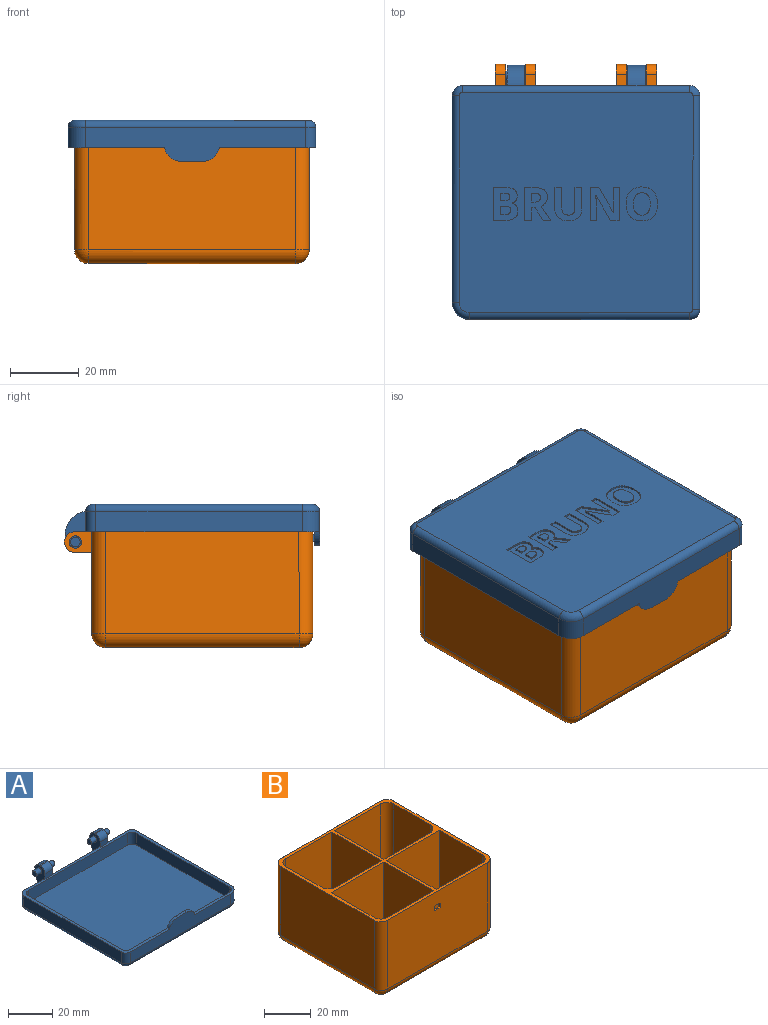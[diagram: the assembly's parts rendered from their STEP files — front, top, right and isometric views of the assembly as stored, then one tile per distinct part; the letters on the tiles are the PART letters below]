
ASSEMBLY  parts=2 mates=1
PART A: 157 faces, bbox 72.7x74.7x14 mm
  f0: plane 13x6mm, normal (0,1,0), area 78mm2, adj f1,f11,f28,f131
  f1: plane 72.3x68.3mm, normal (0,0,1), area 380.4mm2, adj f0,f2,f4,f5,f6,f7,f8,f9
  f2: plane 30.3x6mm, normal (0,1,0), area 181.8mm2, adj f1,f28,f127,f133
  f3: plane 68.3x64.3mm, normal (0,0,-1), area 4104.8mm2, adj f21,f22,f23,f24,f25,f26,f27,f28
  f4: plane 13x6mm, normal (0,1,0), area 78mm2, adj f1,f5,f28,f125
  f5: cylinder r=3mm len=6mm, axis (0,0,1), area 28.3mm2, adj f1,f4,f6,f27
  f6: plane 62.3x6mm, normal (-1,0,0), area 373.8mm2, adj f1,f5,f7,f25
  f7: cylinder r=3mm len=6mm, axis (0,0,1), area 28.3mm2, adj f1,f6,f8,f23
  f8: plane 64.3x10mm, normal (0,-1,0), area 439.9mm2, adj f1,f7,f9,f21,f149,f150,f151
  f9: cylinder r=5mm len=6mm, axis (0,0,1), area 47.1mm2, adj f1,f8,f10,f22
  f10: plane 60.3x6mm, normal (1,0,0), area 361.8mm2, adj f1,f9,f11,f24
  f11: cylinder r=3mm len=6mm, axis (0,0,1), area 28.3mm2, adj f0,f1,f10,f26
  f12: plane 59.3x6.5mm, normal (-1,0,0), area 385.4mm2, adj f1,f13,f19,f20
  f13: cylinder r=3mm len=6.5mm, axis (0,0,1), area 30.6mm2, adj f1,f12,f14,f20
  f14: plane 63.3x6.5mm, normal (0,-1,0), area 411.4mm2, adj f1,f13,f15,f20
  f15: cylinder r=3mm len=6.5mm, axis (0,0,1), area 30.6mm2, adj f1,f14,f16,f20
  f16: plane 59.3x6.5mm, normal (1,0,0), area 385.4mm2, adj f1,f15,f17,f20
  f17: cylinder r=3mm len=6.5mm, axis (0,0,1), area 30.6mm2, adj f1,f16,f18,f20
  f18: plane 63.3x10.5mm, normal (0,1,0), area 459.6mm2, adj f1,f17,f19,f20,f149,f150,f151,f152
  f19: cylinder r=3mm len=6.5mm, axis (0,0,1), area 30.6mm2, adj f1,f12,f18,f20
  f20: plane 69.3x65.3mm, normal (0,0,1), area 4517.6mm2, adj f12,f13,f14,f15,f16,f17,f18,f19
  f21: cylinder r=2mm len=64.3mm, axis (-1,0,0), area 202mm2, adj f3,f8,f22,f23
  f22: torus R=3mm, axis (0,0,1), area 21.1mm2, adj f3,f9,f21,f24
  f23: torus R=1mm, axis (0,0,1), area 11.2mm2, adj f3,f7,f21,f25
  f24: cylinder r=2mm len=60.3mm, axis (0,-1,0), area 189.4mm2, adj f3,f10,f22,f26
  f25: cylinder r=2mm len=62.3mm, axis (0,1,0), area 195.7mm2, adj f3,f6,f23,f27
  f26: torus R=1mm, axis (0,0,1), area 11.2mm2, adj f3,f11,f24,f28
  f27: torus R=1mm, axis (0,0,1), area 11.2mm2, adj f3,f5,f25,f28
  f28: cylinder r=2mm len=66.3mm, axis (1,0,0), area 208.3mm2, adj f0,f2,f3,f4,f26,f27,f147,f148
  f29: plane 6.24x0.5mm, normal (1,0,0), area 3.1mm2, adj f3,f30,f43,f44
  f30: plane 2.04x0.5mm, normal (0,-1,0), area 1mm2, adj f3,f29,f31,f44
  f31: plane 5.89x0.5mm, normal (-1,0,0), area 2.9mm2, adj f3,f30,f32,f44
  f32: extruded ~1.64x0.5mm, area 0.9mm2, adj f3,f31,f33,f44
  f33: extruded ~1.45x0.52mm, area 0.8mm2, adj f3,f32,f34,f44
  f34: extruded ~1.48x0.52mm, area 0.8mm2, adj f3,f33,f35,f44
  f35: extruded ~1.64x0.5mm, area 0.9mm2, adj f3,f34,f36,f44
  f36: plane 5.9x0.5mm, normal (1,0,0), area 3mm2, adj f3,f35,f37,f44
  f37: plane 2.04x0.5mm, normal (0,-1,0), area 1mm2, adj f3,f36,f38,f44
  f38: plane 6.21x0.5mm, normal (-1,0,0), area 3.1mm2, adj f3,f37,f39,f44
  f39: extruded ~2.61x1.03mm, area 1.4mm2, adj f3,f38,f40,f44
  f40: extruded ~2.89x0.95mm, area 1.6mm2, adj f3,f39,f41,f44
  f41: extruded ~2.14x0.5mm, area 1.1mm2, adj f3,f40,f42,f44
  f42: extruded ~1.38x1.23mm, area 0.9mm2, adj f3,f41,f43,f44
  f43: extruded ~1.87x0.5mm, area 1mm2, adj f3,f29,f42,f44
  f44: plane 9.77x7.91mm, normal (0,0,-1), area 42.5mm2, adj f29,f30,f31,f32,f33,f34,f35,f36
  f45: plane 2.51x0.5mm, normal (1,0,0), area 1.3mm2, adj f46,f69,f70,f123
  f46: plane 1.27x0.5mm, normal (0,1,0), area 0.6mm2, adj f45,f47,f70,f123
  f47: extruded ~1.71x1.2mm, area 1.2mm2, adj f46,f48,f70,f123
  f48: extruded ~0.99x0.5mm, area 0.6mm2, adj f47,f49,f70,f123
  f49: extruded ~1.25x0.5mm, area 0.7mm2, adj f48,f69,f70,f123
  f50: plane 1.19x0.5mm, normal (0,-1,0), area 0.6mm2, adj f51,f67,f70,f71
  f51: plane 2.14x0.5mm, normal (1,0,0), area 1.1mm2, adj f50,f52,f70,f71
  f52: plane 1.07x0.5mm, normal (0,1,0), area 0.5mm2, adj f51,f53,f70,f71
  f53: extruded ~1.28x0.5mm, area 0.7mm2, adj f52,f54,f70,f71
  f54: extruded ~0.8x0.5mm, area 0.5mm2, adj f53,f55,f70,f71
  f55: extruded ~0.85x0.5mm, area 0.5mm2, adj f54,f67,f70,f71
  f56: plane 3x0.5mm, normal (0,-1,0), area 1.5mm2, adj f3,f57,f68,f70
  f57: plane 9.64x0.5mm, normal (-1,0,0), area 4.8mm2, adj f3,f56,f58,f70
  f58: plane 3.61x0.5mm, normal (0,1,0), area 1.8mm2, adj f3,f57,f59,f70
  f59: extruded ~2.59x0.74mm, area 1.4mm2, adj f3,f58,f60,f70
  f60: extruded ~2.06x0.95mm, area 1.2mm2, adj f3,f59,f61,f70
  f61: extruded ~1.49x0.5mm, area 0.8mm2, adj f3,f60,f62,f70
  f62: extruded ~1.32x0.76mm, area 0.8mm2, adj f3,f61,f63,f70
  f63: plane 0.5x0.07mm, normal (1,0,0), area 0mm2, adj f3,f62,f64,f70
  f64: extruded ~1.08x0.67mm, area 0.7mm2, adj f3,f63,f65,f70
  f65: extruded ~1.42x0.5mm, area 0.8mm2, adj f3,f64,f66,f70
  f66: extruded ~1.86x0.93mm, area 1.1mm2, adj f3,f65,f68,f70
  f67: extruded ~1.2x0.5mm, area 0.6mm2, adj f50,f55,f70,f71
  f68: extruded ~2.98x0.58mm, area 1.5mm2, adj f3,f56,f66,f70
  f69: plane 1.33x0.5mm, normal (0,-1,0), area 0.7mm2, adj f45,f49,f70,f123
  f70: plane 9.64x7.15mm, normal (0,0,-1), area 50.7mm2, adj f45,f46,f47,f48,f49,f50,f51,f52
  f71: plane 2.76x2.14mm, normal (0,0,-1), area 5.4mm2, adj f50,f51,f52,f53,f54,f55,f67
  f72: extruded ~2.43x0.61mm, area 1.3mm2, adj f73,f85,f86,f124
  f73: extruded ~2.43x0.62mm, area 1.3mm2, adj f72,f74,f86,f124
  f74: extruded ~1.84x0.82mm, area 1mm2, adj f73,f75,f86,f124
  f75: extruded ~3.26x2.43mm, area 2.3mm2, adj f74,f76,f86,f124
  f76: extruded ~3.25x2.45mm, area 2.3mm2, adj f75,f85,f86,f124
  f77: extruded ~3.68x1.19mm, area 2mm2, adj f3,f78,f84,f86
  f78: extruded ~3.68x1.18mm, area 2mm2, adj f3,f77,f79,f86
  f79: extruded ~3.4x1.28mm, area 1.9mm2, adj f3,f78,f80,f86
  f80: extruded ~3.41x1.27mm, area 1.9mm2, adj f3,f79,f81,f86
  f81: extruded ~3.68x1.19mm, area 2mm2, adj f3,f80,f82,f86
  f82: extruded ~3.69x1.19mm, area 2mm2, adj f3,f81,f83,f86
  f83: extruded ~3.4x1.29mm, area 1.9mm2, adj f3,f82,f84,f86
  f84: extruded ~3.4x1.29mm, area 1.9mm2, adj f3,f77,f83,f86
  f85: extruded ~1.83x0.82mm, area 1mm2, adj f72,f76,f86,f124
  f86: plane 9.92x9.18mm, normal (0,0,-1), area 48.6mm2, adj f72,f73,f74,f75,f76,f77,f78,f79
  f87: plane 3.7x0.5mm, normal (1,0,0), area 1.8mm2, adj f3,f88,f105,f106
  f88: plane 1.09x0.5mm, normal (0,1,0), area 0.5mm2, adj f3,f87,f89,f106
  f89: plane 3.7x2.3mm, normal (-0.85,0.53,0), area 2.2mm2, adj f3,f88,f90,f106
  f90: plane 2.27x0.5mm, normal (0,1,0), area 1.1mm2, adj f3,f89,f91,f106
  f91: extruded ~4.2x2.84mm, area 2.5mm2, adj f3,f90,f92,f106
  f92: extruded ~1.33x1.04mm, area 0.9mm2, adj f3,f91,f93,f106
  f93: extruded ~1.51x0.5mm, area 0.8mm2, adj f3,f92,f94,f106
  f94: extruded ~2.17x0.94mm, area 1.2mm2, adj f3,f93,f95,f106
  f95: extruded ~2.91x0.72mm, area 1.5mm2, adj f3,f94,f96,f106
  f96: plane 2.81x0.5mm, normal (0,-1,0), area 1.4mm2, adj f3,f95,f97,f106
  f97: plane 9.64x0.5mm, normal (-1,0,0), area 4.8mm2, adj f3,f96,f105,f106
  f98: plane 0.66x0.5mm, normal (0,-1,0), area 0.3mm2, adj f99,f104,f106,f107
  f99: plane 2.6x0.5mm, normal (1,0,0), area 1.3mm2, adj f98,f100,f106,f107
  f100: plane 0.62x0.5mm, normal (0,1,0), area 0.3mm2, adj f99,f101,f106,f107
  f101: extruded ~1.46x0.5mm, area 0.8mm2, adj f100,f102,f106,f107
  f102: extruded ~0.98x0.5mm, area 0.6mm2, adj f101,f103,f106,f107
  f103: extruded ~1.01x0.5mm, area 0.6mm2, adj f102,f104,f106,f107
  f104: extruded ~1.43x0.5mm, area 0.7mm2, adj f98,f103,f106,f107
  f105: plane 2.04x0.5mm, normal (0,1,0), area 1mm2, adj f3,f87,f97,f106
  f106: plane 9.64x7.7mm, normal (0,0,-1), area 45.4mm2, adj f87,f88,f89,f90,f91,f92,f93,f94
  f107: plane 2.6x2.55mm, normal (0,0,-1), area 5.9mm2, adj f98,f99,f100,f101,f102,f103,f104
  f108: plane 2.6x0.5mm, normal (0,1,0), area 1.3mm2, adj f3,f109,f121,f122
  f109: plane 9.64x0.5mm, normal (1,0,0), area 4.8mm2, adj f3,f108,f110,f122
  f110: plane 1.84x0.5mm, normal (0,-1,0), area 0.9mm2, adj f3,f109,f111,f122
  f111: plane 4.56x0.5mm, normal (-1,0,0), area 2.3mm2, adj f3,f110,f112,f122
  f112: extruded ~2.66x0.5mm, area 1.3mm2, adj f3,f111,f113,f122
  f113: plane 0.5x0.05mm, normal (0,-1,0), area 0mm2, adj f3,f112,f114,f122
  f114: plane 7.22x4.19mm, normal (0.87,-0.5,0), area 4.2mm2, adj f3,f113,f115,f122
  f115: plane 2.58x0.5mm, normal (0,-1,0), area 1.3mm2, adj f3,f114,f116,f122
  f116: plane 9.64x0.5mm, normal (-1,0,0), area 4.8mm2, adj f3,f115,f117,f122
  f117: plane 1.83x0.5mm, normal (0,1,0), area 0.9mm2, adj f3,f116,f118,f122
  f118: plane 4.54x0.5mm, normal (1,0,0), area 2.3mm2, adj f3,f117,f119,f122
  f119: extruded ~2.76x0.5mm, area 1.4mm2, adj f3,f118,f120,f122
  f120: plane 0.5x0.06mm, normal (0,1,0), area 0mm2, adj f3,f119,f121,f122
  f121: plane 7.29x4.19mm, normal (-0.87,0.5,0), area 4.2mm2, adj f3,f108,f120,f122
  f122: plane 9.64x8.55mm, normal (0,0,-1), area 52.6mm2, adj f108,f109,f110,f111,f112,f113,f114,f115
  f123: plane 2.98x2.51mm, normal (0,0,-1), area 6.8mm2, adj f45,f46,f47,f48,f49,f69
  f124: plane 6.51x4.89mm, normal (0,0,-1), area 26.5mm2, adj f72,f73,f74,f75,f76,f85
  f125: plane 12x6.5mm, normal (-1,0,0), area 54.9mm2, adj f1,f4,f126,f128,f129,f137,f138,f139
  f126: plane 5x3mm, normal (0,-1,0), area 15mm2, adj f1,f125,f127,f138
  f127: plane 12x6.5mm, normal (1,0,0), area 54.9mm2, adj f1,f2,f126,f128,f129,f137,f138,f141
  f128: plane 5x2.07mm, normal (0,1,0), area 10.4mm2, adj f125,f127,f137,f148
  f129: plane 5x0.5mm, normal (0,0,1), area 2.5mm2, adj f125,f127,f137,f138
  f130: plane 5x3mm, normal (0,-1,0), area 15mm2, adj f1,f131,f133,f136
  f131: plane 12x6.5mm, normal (1,0,0), area 54.9mm2, adj f0,f1,f130,f132,f134,f135,f136,f143
  f132: plane 5x2.07mm, normal (0,1,0), area 10.4mm2, adj f131,f133,f135,f147
  f133: plane 12x6.5mm, normal (-1,0,0), area 54.9mm2, adj f1,f2,f130,f132,f134,f135,f136,f145
  f134: plane 5x0.5mm, normal (0,0,1), area 2.5mm2, adj f131,f133,f135,f136
  f135: cylinder r=3mm len=5mm, axis (1,0,0), area 23.6mm2, adj f131,f132,f133,f134
  f136: cylinder r=3mm len=5mm, axis (-1,0,0), area 23.6mm2, adj f130,f131,f133,f134
  f137: cylinder r=3mm len=5mm, axis (1,0,0), area 23.6mm2, adj f125,f127,f128,f129
  f138: cylinder r=3mm len=5mm, axis (-1,0,0), area 23.6mm2, adj f125,f126,f127,f129
  f139: cylinder r=1.4mm len=3.4mm, axis (1,0,0), area 29.9mm2, adj f125,f140
  f140: plane 2.8x2.8mm, normal (-1,0,0), area 6.2mm2, adj f139
  f141: cylinder r=1.4mm len=3.4mm, axis (-1,0,0), area 29.9mm2, adj f127,f142
  f142: plane 2.8x2.8mm, normal (1,0,0), area 6.2mm2, adj f141
  f143: cylinder r=1.4mm len=3.4mm, axis (-1,0,0), area 29.9mm2, adj f131,f144
  f144: plane 2.8x2.8mm, normal (1,0,0), area 6.2mm2, adj f143
  f145: cylinder r=1.4mm len=3.4mm, axis (1,0,0), area 29.9mm2, adj f133,f146
  f146: plane 2.8x2.8mm, normal (-1,0,0), area 6.2mm2, adj f145
  f147: cylinder r=7mm len=6.93mm, axis (1,0,0), area 50mm2, adj f28,f131,f132,f133
  f148: cylinder r=7mm len=6.93mm, axis (1,0,0), area 50mm2, adj f28,f125,f127,f128
  f149: plane 6.2x1.5mm, normal (0,0,1), area 9.3mm2, adj f8,f18,f150,f151
  f150: cylinder r=5mm len=4.9mm, axis (0,1,0), area 10.3mm2, adj f1,f8,f18,f149
  f151: cylinder r=5mm len=4.9mm, axis (0,1,0), area 10.3mm2, adj f1,f8,f18,f149
  f152: plane 2x0.8mm, normal (-1,0,0), area 1.6mm2, adj f18,f153,f155,f156
  f153: plane 3x0.8mm, normal (0,0,1), area 2.4mm2, adj f18,f152,f154,f156
  f154: plane 2x0.8mm, normal (1,0,0), area 1.6mm2, adj f18,f153,f155,f156
  f155: plane 3x0.8mm, normal (0,0,-1), area 2.4mm2, adj f18,f152,f154,f156
  f156: plane 3x2mm, normal (0,1,0), area 6mm2, adj f152,f153,f154,f155
PART B: 85 faces, bbox 68.5x72.5x40 mm
  f0: plane 60.5x36mm, normal (0,-1,0), area 2169.8mm2, adj f10,f49,f53,f55,f80,f81,f82,f83
  f1: plane 60.5x36mm, normal (0,1,0), area 2106mm2, adj f10,f44,f46,f47,f56,f57,f58,f59
  f2: plane 38.5x32mm, normal (0,-1,0), area 1228.6mm2, adj f5,f10,f19,f29,f40
  f3: plane 28x23.5mm, normal (0,1,0), area 658mm2, adj f4,f10,f29,f38
  f4: cylinder r=15mm len=28mm, axis (1,0,0), area 659.7mm2, adj f3,f5,f29,f39
  f5: plane 28x15mm, normal (0,0,1), area 420mm2, adj f2,f4,f29,f40
  f6: plane 38.5x28mm, normal (0,-1,0), area 1078mm2, adj f9,f10,f26,f32
  f7: plane 28x23.5mm, normal (0,1,0), area 658mm2, adj f8,f10,f26,f30
  f8: cylinder r=15mm len=28mm, axis (1,0,0), area 659.7mm2, adj f7,f9,f26,f31
  f9: plane 28x15mm, normal (0,0,1), area 420mm2, adj f6,f8,f26,f33
  f10: plane 68.5x64.5mm, normal (0,0,1), area 585.1mm2, adj f0,f1,f2,f3,f6,f7,f11,f12
  f11: plane 56.5x36mm, normal (1,0,0), area 2034mm2, adj f10,f46,f52,f55
  f12: plane 56.5x36mm, normal (-1,0,0), area 2034mm2, adj f10,f44,f48,f49
  f13: plane 60.5x56.5mm, normal (0,0,-1), area 3418.2mm2, adj f47,f48,f52,f53
  f14: plane 38.5x32mm, normal (0,-1,0), area 1228.6mm2, adj f10,f17,f18,f28,f43
  f15: plane 28x23.5mm, normal (0,1,0), area 658mm2, adj f10,f16,f28,f41
  f16: cylinder r=15mm len=28mm, axis (1,0,0), area 659.7mm2, adj f15,f17,f28,f42
  f17: plane 28x15mm, normal (0,0,1), area 420mm2, adj f14,f16,f28,f43
  f18: plane 34.5x26mm, normal (1,0,0), area 871mm2, adj f10,f14,f41,f42,f43
  f19: plane 34.5x26mm, normal (-1,0,0), area 871mm2, adj f2,f10,f38,f39,f40
  f20: plane 38.5x28mm, normal (0,-1,0), area 1078mm2, adj f10,f23,f27,f36
  f21: plane 28x23.5mm, normal (0,1,0), area 658mm2, adj f10,f22,f27,f34
  f22: cylinder r=15mm len=28mm, axis (1,0,0), area 659.7mm2, adj f21,f23,f27,f35
  f23: plane 28x15mm, normal (0,0,1), area 420mm2, adj f20,f22,f27,f37
  f24: plane 34.5x22mm, normal (1,0,0), area 733mm2, adj f10,f34,f35,f36,f37
  f25: plane 34.5x22mm, normal (-1,0,0), area 733mm2, adj f10,f30,f31,f32,f33
  f26: plane 38.5x30mm, normal (1,0,0), area 1106.7mm2, adj f6,f7,f8,f9,f10
  f27: plane 38.5x30mm, normal (-1,0,0), area 1106.7mm2, adj f10,f20,f21,f22,f23
  f28: plane 38.5x30mm, normal (-1,0,0), area 1106.7mm2, adj f10,f14,f15,f16,f17
  f29: plane 38.5x30mm, normal (1,0,0), area 1106.7mm2, adj f2,f3,f4,f5,f10
  f30: cylinder r=4mm len=23.5mm, axis (0,0,1), area 147.7mm2, adj f7,f10,f25,f31
  f31: torus R=11mm, axis (1,0,0), area 133.7mm2, adj f8,f25,f30,f33
  f32: cylinder r=4mm len=38.5mm, axis (0,0,-1), area 232.8mm2, adj f6,f10,f25,f33
  f33: cylinder r=4mm len=15mm, axis (0,-1,0), area 85.1mm2, adj f9,f25,f31,f32
  f34: cylinder r=4mm len=23.5mm, axis (0,0,-1), area 147.7mm2, adj f10,f21,f24,f35
  f35: torus R=11mm, axis (1,0,0), area 133.7mm2, adj f22,f24,f34,f37
  f36: cylinder r=4mm len=38.5mm, axis (0,0,1), area 232.8mm2, adj f10,f20,f24,f37
  f37: cylinder r=4mm len=15mm, axis (0,1,0), area 85.1mm2, adj f23,f24,f35,f36
  f38: cylinder r=4mm len=23.5mm, axis (0,0,1), area 147.7mm2, adj f3,f10,f19,f39
  f39: torus R=11mm, axis (1,0,0), area 133.7mm2, adj f4,f19,f38,f40
  f40: cylinder r=4mm len=15mm, axis (0,-1,0), area 94.2mm2, adj f2,f5,f19,f39
  f41: cylinder r=4mm len=23.5mm, axis (0,0,-1), area 147.7mm2, adj f10,f15,f18,f42
  f42: torus R=11mm, axis (1,0,0), area 133.7mm2, adj f16,f18,f41,f43
  f43: cylinder r=4mm len=15mm, axis (0,1,0), area 94.2mm2, adj f14,f17,f18,f42
  f44: cylinder r=4mm len=36mm, axis (0,0,-1), area 226.2mm2, adj f1,f10,f12,f45
  f45: sphere r=4mm, area 25.1mm2, adj f44,f47,f48
  f46: cylinder r=4mm len=36mm, axis (0,0,1), area 226.2mm2, adj f1,f10,f11,f50
  f47: cylinder r=4mm len=60.5mm, axis (1,0,0), area 380.1mm2, adj f1,f13,f45,f50
  f48: cylinder r=4mm len=56.5mm, axis (0,1,0), area 355mm2, adj f12,f13,f45,f51
  f49: cylinder r=4mm len=36mm, axis (0,0,1), area 226.2mm2, adj f0,f10,f12,f51
  f50: sphere r=4mm, area 25.1mm2, adj f46,f47,f52
  f51: sphere r=4mm, area 25.1mm2, adj f48,f49,f53
  f52: cylinder r=4mm len=56.5mm, axis (0,-1,0), area 355mm2, adj f11,f13,f50,f54
  f53: cylinder r=4mm len=60.5mm, axis (-1,0,0), area 380.1mm2, adj f0,f13,f51,f54
  f54: sphere r=4mm, area 25.1mm2, adj f52,f53,f55
  f55: cylinder r=4mm len=36mm, axis (0,0,-1), area 226.2mm2, adj f0,f10,f11,f54
  f56: plane 8x6mm, normal (-1,0,0), area 34mm2, adj f1,f58,f59,f75,f79
  f57: plane 8x6mm, normal (1,0,0), area 34mm2, adj f1,f58,f59,f75,f79
  f58: plane 5x3mm, normal (0,0,-1), area 15mm2, adj f1,f56,f57,f79
  f59: plane 5x3mm, normal (0,0,1), area 15mm2, adj f1,f56,f57,f79
  f60: plane 8x6mm, normal (-1,0,0), area 34mm2, adj f1,f62,f63,f74,f78
  f61: plane 8x6mm, normal (1,0,0), area 34mm2, adj f1,f62,f63,f74,f78
  f62: plane 5x3mm, normal (0,0,-1), area 15mm2, adj f1,f60,f61,f78
  f63: plane 5x3mm, normal (0,0,1), area 15mm2, adj f1,f60,f61,f78
  f64: plane 8x6mm, normal (-1,0,0), area 34mm2, adj f1,f66,f67,f73,f77
  f65: plane 8x6mm, normal (1,0,0), area 34mm2, adj f1,f66,f67,f73,f77
  f66: plane 5x3mm, normal (0,0,-1), area 15mm2, adj f1,f64,f65,f77
  f67: plane 5x3mm, normal (0,0,1), area 15mm2, adj f1,f64,f65,f77
  f68: plane 8x6mm, normal (-1,0,0), area 34mm2, adj f1,f70,f71,f72,f76
  f69: plane 8x6mm, normal (1,0,0), area 34mm2, adj f1,f70,f71,f72,f76
  f70: plane 5x3mm, normal (0,0,-1), area 15mm2, adj f1,f68,f69,f76
  f71: plane 5x3mm, normal (0,0,1), area 15mm2, adj f1,f68,f69,f76
  f72: cylinder r=1.8mm len=3.6mm, axis (1,0,0), area 33.9mm2, adj f68,f69
  f73: cylinder r=1.8mm len=3.6mm, axis (1,0,0), area 33.9mm2, adj f64,f65
  f74: cylinder r=1.8mm len=3.6mm, axis (1,0,0), area 33.9mm2, adj f60,f61
  f75: cylinder r=1.8mm len=3.6mm, axis (1,0,0), area 33.9mm2, adj f56,f57
  f76: cylinder r=3mm len=6mm, axis (1,0,0), area 28.3mm2, adj f68,f69,f70,f71
  f77: cylinder r=3mm len=6mm, axis (1,0,0), area 28.3mm2, adj f64,f65,f66,f67
  f78: cylinder r=3mm len=6mm, axis (1,0,0), area 28.3mm2, adj f60,f61,f62,f63
  f79: cylinder r=3mm len=6mm, axis (1,0,0), area 28.3mm2, adj f56,f57,f58,f59
  f80: plane 3.4x0.75mm, normal (0,0,1), area 2.6mm2, adj f0,f81,f83,f84
  f81: plane 2.4x0.75mm, normal (-1,0,0), area 1.8mm2, adj f0,f80,f82,f84
  f82: plane 3.4x0.75mm, normal (0,0,-1), area 2.6mm2, adj f0,f81,f83,f84
  f83: plane 2.4x0.75mm, normal (1,0,0), area 1.8mm2, adj f0,f80,f82,f84
  f84: plane 3.4x2.4mm, normal (0,-1,0), area 8.2mm2, adj f80,f81,f82,f83
PLACE A rot(axis=(0,-1,0),180deg) t=(-39.91,-89.31,-60.81)mm
PLACE B rot(axis=(-0.18,0.89,-0.42),0deg) t=(-39.9,-89.21,-54.62)mm
MATE revolute A.f135 <-> B.f72  axis (1,0,0) through (-16.35,-52.17,-63.84)mm
